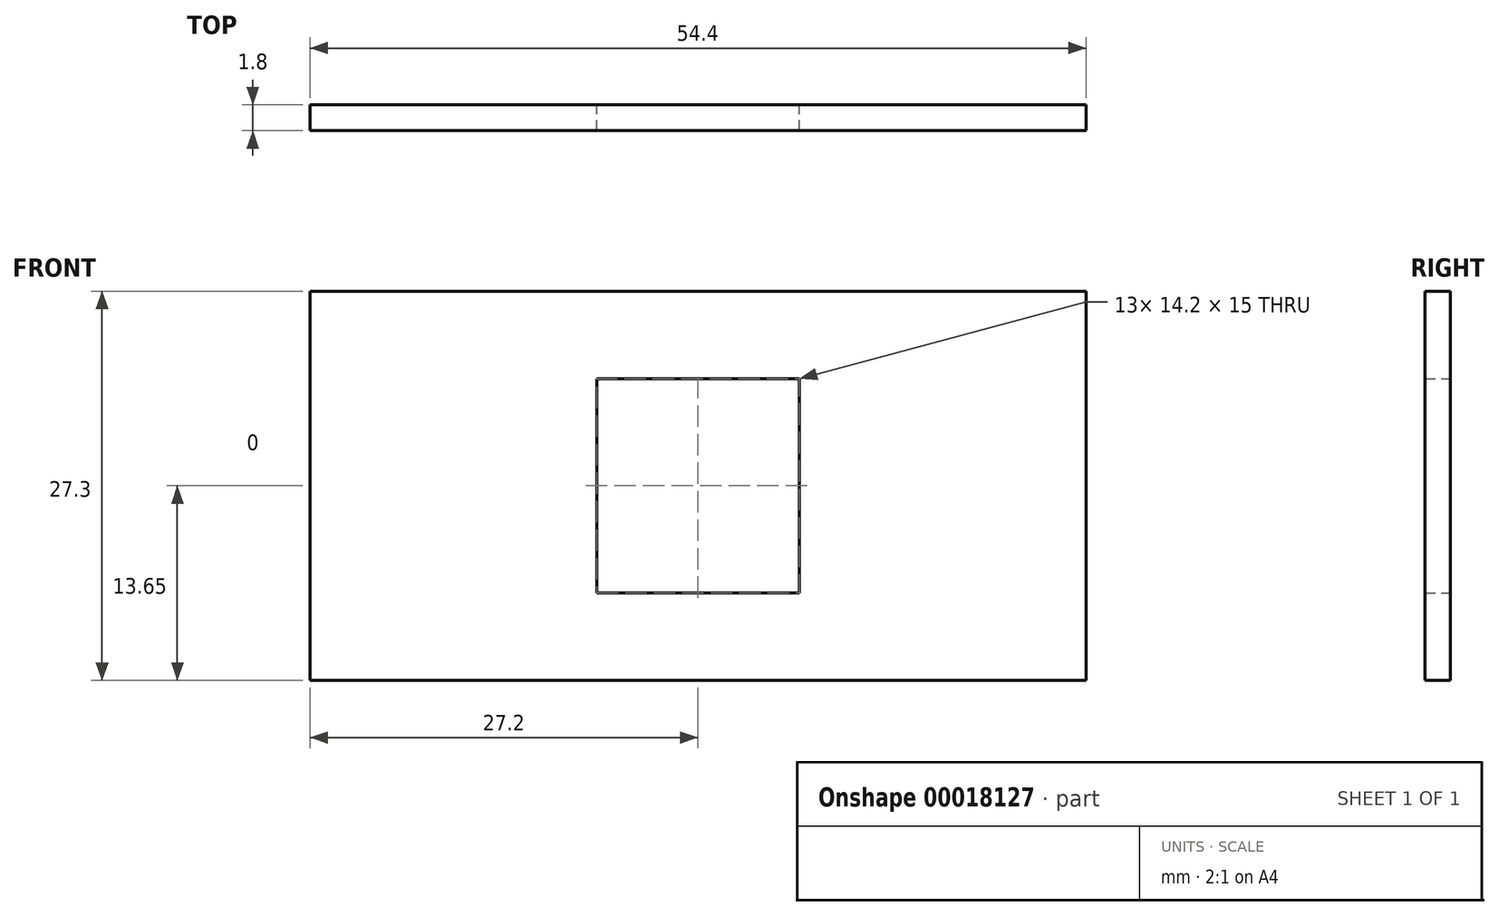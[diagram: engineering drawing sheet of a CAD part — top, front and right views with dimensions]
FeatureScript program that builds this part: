
annotation { "Feature Type Name" : "Feature", "Feature Type Description" : "" }
export const myFeature = defineFeature(function(context is Context, id is Id, definition is map)
    precondition{}
    {
        {
            var Q0;
            Q0=qCreatedBy(makeId("Front.planeOp"),FACE);
            var sketch = newSketch(context, id + "F0", { "sketchPlane" : qUnion([Q0])});
            skLineSegment(sketch, "E0.bottom", {"start": v(0, 0) * mm, "end": v(54.4, 0) * mm});
            skLineSegment(sketch, "E0.top", {"start": v(0, 27.3) * mm, "end": v(54.4, 27.3) * mm});
            skLineSegment(sketch, "E0.left", {"start": v(0, 0) * mm, "end": v(0, 27.3) * mm});
            skLineSegment(sketch, "E0.right", {"start": v(54.4, 0) * mm, "end": v(54.4, 27.3) * mm});
            skLineSegment(sketch, "E1", {"start": v(0, 22.3) * mm, "end": v(54.4, 22.3) * mm, "construction": true});
            skLineSegment(sketch, "E2", {"start": v(0, 5) * mm, "end": v(54.4, 5) * mm, "construction": true});
            skLineSegment(sketch, "E3", {"start": v(5, 27.3) * mm, "end": v(5, 0) * mm, "construction": true});
            skLineSegment(sketch, "E4", {"start": v(49.4, 27.3) * mm, "end": v(49.4, 0) * mm, "construction": true});
            skLineSegment(sketch, "E5.bottom", {"start": v(20.1, 21.15) * mm, "end": v(34.3, 21.15) * mm});
            skLineSegment(sketch, "E5.top", {"start": v(20.1, 6.15) * mm, "end": v(34.3, 6.15) * mm});
            skLineSegment(sketch, "E5.left", {"start": v(20.1, 21.15) * mm, "end": v(20.1, 6.15) * mm});
            skLineSegment(sketch, "E5.right", {"start": v(34.3, 21.15) * mm, "end": v(34.3, 6.15) * mm});
            skSolve(sketch);
        }
        {
            var Q0;
            Q0=makeQuery(id+"F0.imprint","IMPRINT",FACE,{"disambiguationData":[TD([[makeQuery(id+"F0.imprint","IMPRINT",EDGE,{"derivedFrom":sQuery(id+"F0.wireOp",EDGE,"E0.bottom")}),1.0]])]});
            extrude(context, id + "F1", {"entities" : qUnion([Q0]), "depth" : 1.8 * mm});
        }
    });
